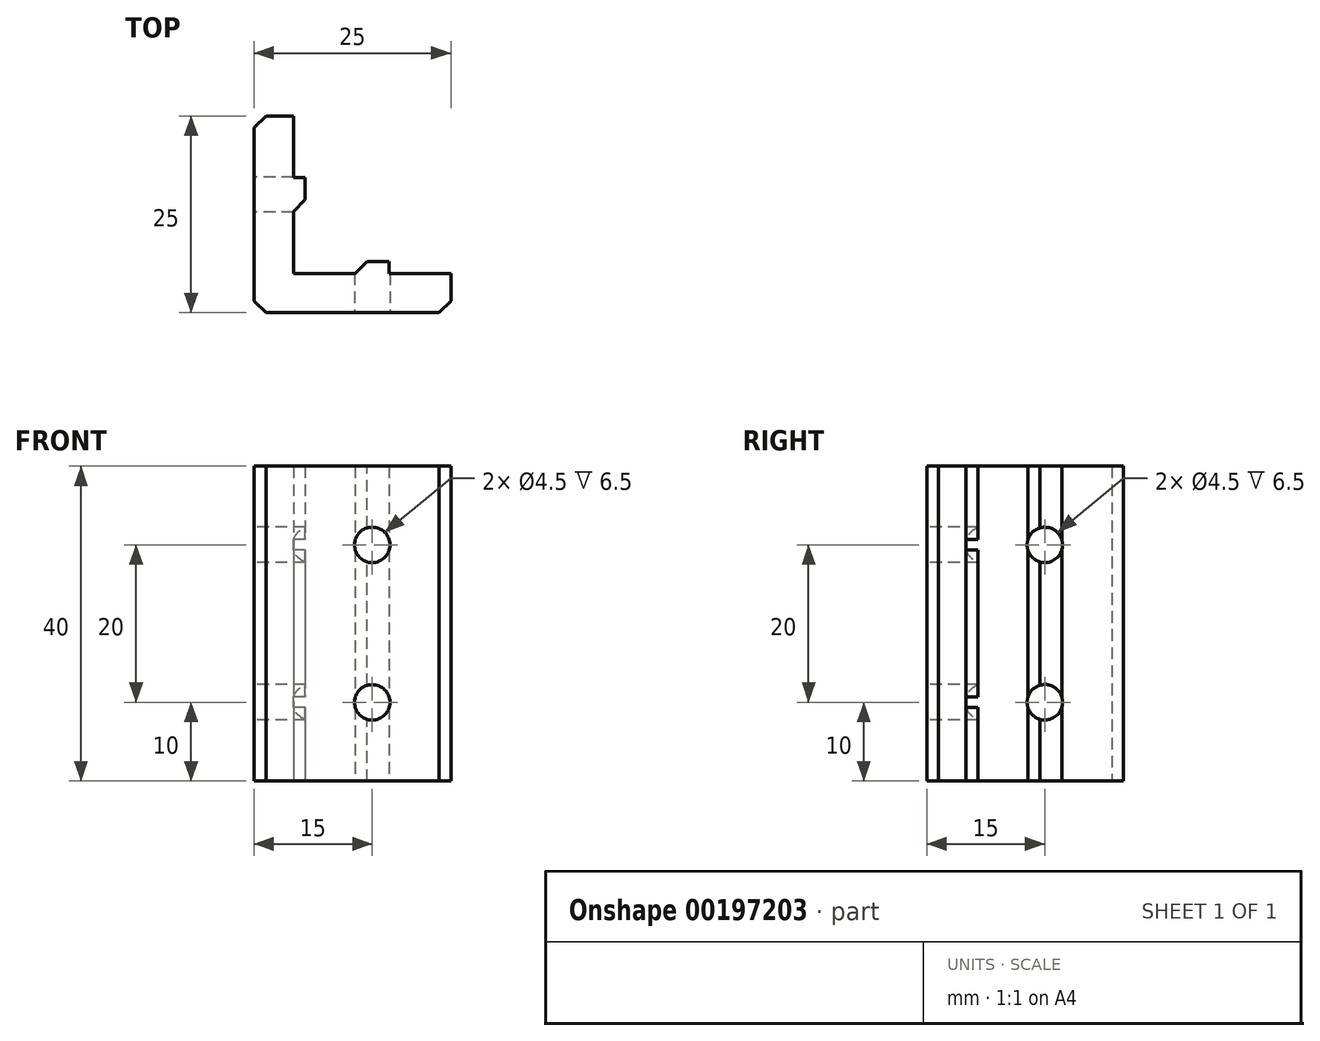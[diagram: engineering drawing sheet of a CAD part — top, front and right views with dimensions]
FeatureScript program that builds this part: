
annotation { "Feature Type Name" : "Feature", "Feature Type Description" : "" }
export const myFeature = defineFeature(function(context is Context, id is Id, definition is map)
    precondition{}
    {
        {
            var Q0;
            Q0=qCreatedBy(makeId("Top.planeOp"),FACE);
            var sketch = newSketch(context, id + "F0", { "sketchPlane" : qUnion([Q0])});
            skLineSegment(sketch, "E0", {"start": v(0, 0) * mm, "end": v(25, 0) * mm});
            skLineSegment(sketch, "E1", {"start": v(25, 0) * mm, "end": v(25, 5) * mm});
            skLineSegment(sketch, "E2", {"start": v(25, 5) * mm, "end": v(5, 5) * mm});
            skLineSegment(sketch, "E3", {"start": v(5, 5) * mm, "end": v(5, 25) * mm});
            skLineSegment(sketch, "E4", {"start": v(5, 25) * mm, "end": v(0, 25) * mm});
            skLineSegment(sketch, "E5", {"start": v(0, 25) * mm, "end": v(0, 0) * mm});
            skLineSegment(sketch, "E6", {"start": v(12.85, 5) * mm, "end": v(12.85, 6.5) * mm});
            skLineSegment(sketch, "E7", {"start": v(12.85, 6.5) * mm, "end": v(17.15, 6.5) * mm});
            skLineSegment(sketch, "E8", {"start": v(17.15, 6.5) * mm, "end": v(17.15, 5) * mm});
            skLineSegment(sketch, "E9", {"start": v(5, 17.15) * mm, "end": v(6.5, 17.15) * mm});
            skLineSegment(sketch, "E10", {"start": v(6.5, 17.15) * mm, "end": v(6.5, 12.85) * mm});
            skLineSegment(sketch, "E11", {"start": v(6.5, 12.85) * mm, "end": v(5, 12.85) * mm});
            skSolve(sketch);
        }
        {
            var Q0;
            Q0=makeQuery(id+"F0.imprint","IMPRINT",FACE,{"disambiguationData":[TD([[makeQuery(id+"F0.imprint","IMPRINT",EDGE,{"derivedFrom":sQuery(id+"F0.wireOp",EDGE,"E0")}),1.0]])]});
            var Q1;
            {var subQ0=sQuery(id+"F0.wireOp",EDGE,"E9");Q1=makeQuery(id+"F0.imprint","IMPRINT",FACE,{"disambiguationData":[TD([[makeQuery(id+"F0.imprint","IMPRINT",EDGE,{"derivedFrom":subQ0}),-1.0]])]});}
            var Q2;
            {var subQ0=sQuery(id+"F0.wireOp",EDGE,"E6");Q2=makeQuery(id+"F0.imprint","IMPRINT",FACE,{"disambiguationData":[TD([[makeQuery(id+"F0.imprint","IMPRINT",EDGE,{"derivedFrom":subQ0}),-1.0]])]});}
            extrude(context, id + "F1", {"entities" : qUnion([Q0, Q1, Q2]), "depth" : 40 * mm});
        }
        {
            var Q0;
            Q0=makeQuery(id+"F1.opExtrude","SWEPT_FACE",FACE,{"disambiguationData":[OSD([sQuery(id+"F0.wireOp",EDGE,"E0")])]});
            var sketch = newSketch(context, id + "F2", { "sketchPlane" : qUnion([Q0])});
            skCircle(sketch, "E12", {"center": v(15, 30) * mm, "radius": 2.25 * mm});
            skCircle(sketch, "E13", {"center": v(15, 10) * mm, "radius": 2.25 * mm});
            skSolve(sketch);
        }
        {
            var Q0;
            Q0=makeQuery(id+"F2.imprint","IMPRINT",FACE,{"disambiguationData":[TD([[makeQuery(id+"F2.imprint","IMPRINT",EDGE,{"derivedFrom":sQuery(id+"F2.wireOp",EDGE,"E12")}),1.0]])]});
            var Q1;
            Q1=makeQuery(id+"F2.imprint","IMPRINT",FACE,{"disambiguationData":[TD([[makeQuery(id+"F2.imprint","IMPRINT",EDGE,{"derivedFrom":sQuery(id+"F2.wireOp",EDGE,"E13")}),1.0]])]});
            extrude(context, id + "F3", {"entities" : qUnion([Q0, Q1]), "operationType" : NewBodyOperationType.REMOVE, "endBound" : BoundingType.UP_TO_NEXT, "oppositeDirection" : true, "depth" : 25 * mm});
        }
        {
            var Q0;
            Q0=makeQuery(id+"F1.opExtrude","SWEPT_FACE",FACE,{"disambiguationData":[OSD([sQuery(id+"F0.wireOp",EDGE,"E5")])]});
            var sketch = newSketch(context, id + "F4", { "sketchPlane" : qUnion([Q0])});
            skCircle(sketch, "E14", {"center": v(-15, 30) * mm, "radius": 2.25 * mm});
            skCircle(sketch, "E15", {"center": v(-15, 10) * mm, "radius": 2.25 * mm});
            skSolve(sketch);
        }
        {
            var Q0;
            Q0=makeQuery(id+"F4.imprint","IMPRINT",FACE,{"disambiguationData":[TD([[makeQuery(id+"F4.imprint","IMPRINT",EDGE,{"derivedFrom":sQuery(id+"F4.wireOp",EDGE,"E14")}),1.0]])]});
            var Q1;
            Q1=makeQuery(id+"F4.imprint","IMPRINT",FACE,{"disambiguationData":[TD([[makeQuery(id+"F4.imprint","IMPRINT",EDGE,{"derivedFrom":sQuery(id+"F4.wireOp",EDGE,"E15")}),1.0]])]});
            extrude(context, id + "F5", {"entities" : qUnion([Q0, Q1]), "operationType" : NewBodyOperationType.REMOVE, "endBound" : BoundingType.UP_TO_NEXT, "oppositeDirection" : true, "depth" : 25 * mm});
        }
        {
            var Q0;
            {var subQ0=sQuery(id+"F0.wireOp",EDGE,"E6");var subQ1=sQuery(id+"F0.wireOp",EDGE,"E7");Q0=makeQuery(id+"F3.boolean.opBoolean","SPLIT",EDGE,{"disambiguationData":[TD([makeQuery(id+"F1.opExtrude","SWEPT_FACE",FACE,{"disambiguationData":[OSD([subQ0])]}),makeQuery(id+"F1.opExtrude","SWEPT_FACE",FACE,{"disambiguationData":[OSD([subQ1])]}),makeQuery(id+"F3.opExtrude","SWEPT_FACE",FACE,{"disambiguationData":[OSD([sQuery(id+"F2.wireOp",EDGE,"E12")])]}),makeQuery(id+"F3.opExtrude","SWEPT_FACE",FACE,{"disambiguationData":[OSD([sQuery(id+"F2.wireOp",EDGE,"E13")])]})])],"derivedFrom":makeQuery(id+"F1.opExtrude","SWEPT_EDGE",EDGE,{"disambiguationData":[OSD([subQ0,subQ1])]})});}
            var Q1;
            {var subQ0=sQuery(id+"F0.wireOp",EDGE,"E7");var subQ1=sQuery(id+"F0.wireOp",EDGE,"E6");Q1=makeQuery(id+"F3.boolean.opBoolean","SPLIT",EDGE,{"disambiguationData":[TD([makeQuery(id+"F1.opExtrude","CAP_FACE",FACE,{"disambiguationData":[OSD([sQuery(id+"F0.wireOp",EDGE,"E0"),sQuery(id+"F0.wireOp",EDGE,"E1"),sQuery(id+"F0.wireOp",EDGE,"E2"),sQuery(id+"F0.wireOp",EDGE,"E3"),sQuery(id+"F0.wireOp",EDGE,"E4"),sQuery(id+"F0.wireOp",EDGE,"E5"),subQ1,subQ0,sQuery(id+"F0.wireOp",EDGE,"E8"),sQuery(id+"F0.wireOp",EDGE,"E9"),sQuery(id+"F0.wireOp",EDGE,"E10"),sQuery(id+"F0.wireOp",EDGE,"E11")])],"isStart":false}),makeQuery(id+"F1.opExtrude","SWEPT_FACE",FACE,{"disambiguationData":[OSD([subQ1])]}),makeQuery(id+"F1.opExtrude","SWEPT_FACE",FACE,{"disambiguationData":[OSD([subQ0])]}),makeQuery(id+"F3.opExtrude","SWEPT_FACE",FACE,{"disambiguationData":[OSD([sQuery(id+"F2.wireOp",EDGE,"E12")])]})])],"derivedFrom":makeQuery(id+"F1.opExtrude","SWEPT_EDGE",EDGE,{"disambiguationData":[OSD([subQ1,subQ0])]})});}
            var Q2;
            {var subQ0=sQuery(id+"F0.wireOp",EDGE,"E7");var subQ1=sQuery(id+"F0.wireOp",EDGE,"E6");Q2=makeQuery(id+"F3.boolean.opBoolean","SPLIT",EDGE,{"disambiguationData":[TD([makeQuery(id+"F1.opExtrude","CAP_FACE",FACE,{"disambiguationData":[OSD([sQuery(id+"F0.wireOp",EDGE,"E0"),sQuery(id+"F0.wireOp",EDGE,"E1"),sQuery(id+"F0.wireOp",EDGE,"E2"),sQuery(id+"F0.wireOp",EDGE,"E3"),sQuery(id+"F0.wireOp",EDGE,"E4"),sQuery(id+"F0.wireOp",EDGE,"E5"),subQ1,subQ0,sQuery(id+"F0.wireOp",EDGE,"E8"),sQuery(id+"F0.wireOp",EDGE,"E9"),sQuery(id+"F0.wireOp",EDGE,"E10"),sQuery(id+"F0.wireOp",EDGE,"E11")])],"isStart":true}),makeQuery(id+"F1.opExtrude","SWEPT_FACE",FACE,{"disambiguationData":[OSD([subQ1])]}),makeQuery(id+"F1.opExtrude","SWEPT_FACE",FACE,{"disambiguationData":[OSD([subQ0])]}),makeQuery(id+"F3.opExtrude","SWEPT_FACE",FACE,{"disambiguationData":[OSD([sQuery(id+"F2.wireOp",EDGE,"E13")])]})])],"derivedFrom":makeQuery(id+"F1.opExtrude","SWEPT_EDGE",EDGE,{"disambiguationData":[OSD([subQ1,subQ0])]})});}
            var Q3;
            {var subQ0=sQuery(id+"F0.wireOp",EDGE,"E11");var subQ1=sQuery(id+"F0.wireOp",EDGE,"E10");Q3=makeQuery(id+"F5.boolean.opBoolean","SPLIT",EDGE,{"disambiguationData":[TD([makeQuery(id+"F1.opExtrude","CAP_FACE",FACE,{"disambiguationData":[OSD([sQuery(id+"F0.wireOp",EDGE,"E0"),sQuery(id+"F0.wireOp",EDGE,"E1"),sQuery(id+"F0.wireOp",EDGE,"E2"),sQuery(id+"F0.wireOp",EDGE,"E3"),sQuery(id+"F0.wireOp",EDGE,"E4"),sQuery(id+"F0.wireOp",EDGE,"E5"),sQuery(id+"F0.wireOp",EDGE,"E6"),sQuery(id+"F0.wireOp",EDGE,"E7"),sQuery(id+"F0.wireOp",EDGE,"E8"),sQuery(id+"F0.wireOp",EDGE,"E9"),subQ1,subQ0])],"isStart":true}),makeQuery(id+"F1.opExtrude","SWEPT_FACE",FACE,{"disambiguationData":[OSD([subQ1])]}),makeQuery(id+"F1.opExtrude","SWEPT_FACE",FACE,{"disambiguationData":[OSD([subQ0])]}),makeQuery(id+"F5.opExtrude","SWEPT_FACE",FACE,{"disambiguationData":[OSD([sQuery(id+"F4.wireOp",EDGE,"E15")])]})])],"derivedFrom":makeQuery(id+"F1.opExtrude","SWEPT_EDGE",EDGE,{"disambiguationData":[OSD([subQ1,subQ0])]})});}
            var Q4;
            {var subQ0=sQuery(id+"F0.wireOp",EDGE,"E10");var subQ1=sQuery(id+"F0.wireOp",EDGE,"E11");Q4=makeQuery(id+"F5.boolean.opBoolean","SPLIT",EDGE,{"disambiguationData":[TD([makeQuery(id+"F1.opExtrude","SWEPT_FACE",FACE,{"disambiguationData":[OSD([subQ0])]}),makeQuery(id+"F1.opExtrude","SWEPT_FACE",FACE,{"disambiguationData":[OSD([subQ1])]}),makeQuery(id+"F5.opExtrude","SWEPT_FACE",FACE,{"disambiguationData":[OSD([sQuery(id+"F4.wireOp",EDGE,"E14")])]}),makeQuery(id+"F5.opExtrude","SWEPT_FACE",FACE,{"disambiguationData":[OSD([sQuery(id+"F4.wireOp",EDGE,"E15")])]})])],"derivedFrom":makeQuery(id+"F1.opExtrude","SWEPT_EDGE",EDGE,{"disambiguationData":[OSD([subQ0,subQ1])]})});}
            var Q5;
            {var subQ0=sQuery(id+"F0.wireOp",EDGE,"E11");var subQ1=sQuery(id+"F0.wireOp",EDGE,"E10");Q5=makeQuery(id+"F5.boolean.opBoolean","SPLIT",EDGE,{"disambiguationData":[TD([makeQuery(id+"F1.opExtrude","CAP_FACE",FACE,{"disambiguationData":[OSD([sQuery(id+"F0.wireOp",EDGE,"E0"),sQuery(id+"F0.wireOp",EDGE,"E1"),sQuery(id+"F0.wireOp",EDGE,"E2"),sQuery(id+"F0.wireOp",EDGE,"E3"),sQuery(id+"F0.wireOp",EDGE,"E4"),sQuery(id+"F0.wireOp",EDGE,"E5"),sQuery(id+"F0.wireOp",EDGE,"E6"),sQuery(id+"F0.wireOp",EDGE,"E7"),sQuery(id+"F0.wireOp",EDGE,"E8"),sQuery(id+"F0.wireOp",EDGE,"E9"),subQ1,subQ0])],"isStart":false}),makeQuery(id+"F1.opExtrude","SWEPT_FACE",FACE,{"disambiguationData":[OSD([subQ1])]}),makeQuery(id+"F1.opExtrude","SWEPT_FACE",FACE,{"disambiguationData":[OSD([subQ0])]}),makeQuery(id+"F5.opExtrude","SWEPT_FACE",FACE,{"disambiguationData":[OSD([sQuery(id+"F4.wireOp",EDGE,"E14")])]})])],"derivedFrom":makeQuery(id+"F1.opExtrude","SWEPT_EDGE",EDGE,{"disambiguationData":[OSD([subQ1,subQ0])]})});}
            var Q6;
            {var subQ0=sQuery(id+"F2.wireOp",EDGE,"E12");Q6=makeQuery(id+"F3.boolean.opBoolean","COPY",EDGE,{"derivedFrom":makeQuery(id+"F3.opExtrude","CAP_EDGE",EDGE,{"disambiguationData":[OSD([subQ0]),topologyDisambiguationEdgeConnected([makeQuery(id+"F1.opExtrude","SWEPT_FACE",FACE,{"disambiguationData":[OSD([sQuery(id+"F0.wireOp",EDGE,"E7")])]}),makeQuery(id+"F2.imprint","IMPRINT",EDGE,{"derivedFrom":subQ0})]),OD(1.0)],"isStart":false})});}
            var Q7;
            Q7=makeQuery(id+"F3.boolean.opBoolean","COPY",EDGE,{"derivedFrom":makeQuery(id+"F3.opExtrude","CAP_EDGE",EDGE,{"disambiguationData":[OSD([sQuery(id+"F2.wireOp",EDGE,"E13")]),topologyDisambiguationEdgeConnected([makeQuery(id+"F1.opExtrude","SWEPT_FACE",FACE,{"disambiguationData":[OSD([sQuery(id+"F0.wireOp",EDGE,"E7")])]})]),OD(1.0)],"isStart":false})});
            var Q8;
            Q8=makeQuery(id+"F5.boolean.opBoolean","COPY",EDGE,{"derivedFrom":makeQuery(id+"F5.opExtrude","CAP_EDGE",EDGE,{"disambiguationData":[OSD([sQuery(id+"F4.wireOp",EDGE,"E15")]),topologyDisambiguationEdgeConnected([makeQuery(id+"F1.opExtrude","SWEPT_FACE",FACE,{"disambiguationData":[OSD([sQuery(id+"F0.wireOp",EDGE,"E10")])]})]),OD(1.0)],"isStart":false})});
            var Q9;
            {var subQ0=sQuery(id+"F4.wireOp",EDGE,"E14");Q9=makeQuery(id+"F5.boolean.opBoolean","COPY",EDGE,{"derivedFrom":makeQuery(id+"F5.opExtrude","CAP_EDGE",EDGE,{"disambiguationData":[OSD([subQ0]),topologyDisambiguationEdgeConnected([makeQuery(id+"F1.opExtrude","SWEPT_FACE",FACE,{"disambiguationData":[OSD([sQuery(id+"F0.wireOp",EDGE,"E10")])]}),makeQuery(id+"F4.imprint","IMPRINT",EDGE,{"derivedFrom":subQ0})]),OD(1.0)],"isStart":false})});}
            var Q10;
            Q10=makeQuery(id+"F1.opExtrude","SWEPT_EDGE",EDGE,{"disambiguationData":[OSD([sQuery(id+"F0.wireOp",EDGE,"E0"),sQuery(id+"F0.wireOp",EDGE,"E5")])]});
            var Q11;
            Q11=makeQuery(id+"F1.opExtrude","SWEPT_EDGE",EDGE,{"disambiguationData":[OSD([sQuery(id+"F0.wireOp",EDGE,"E0"),sQuery(id+"F0.wireOp",EDGE,"E1")])]});
            var Q12;
            Q12=makeQuery(id+"F1.opExtrude","SWEPT_EDGE",EDGE,{"disambiguationData":[OSD([sQuery(id+"F0.wireOp",EDGE,"E4"),sQuery(id+"F0.wireOp",EDGE,"E5")])]});
            chamfer(context, id + "F6", {"entities" : qUnion([Q0, Q1, Q2, Q3, Q4, Q5, Q6, Q7, Q8, Q9, Q10, Q11, Q12]), "width" : 1.5 * mm, "tangentPropagation" : true});
        }
    });
